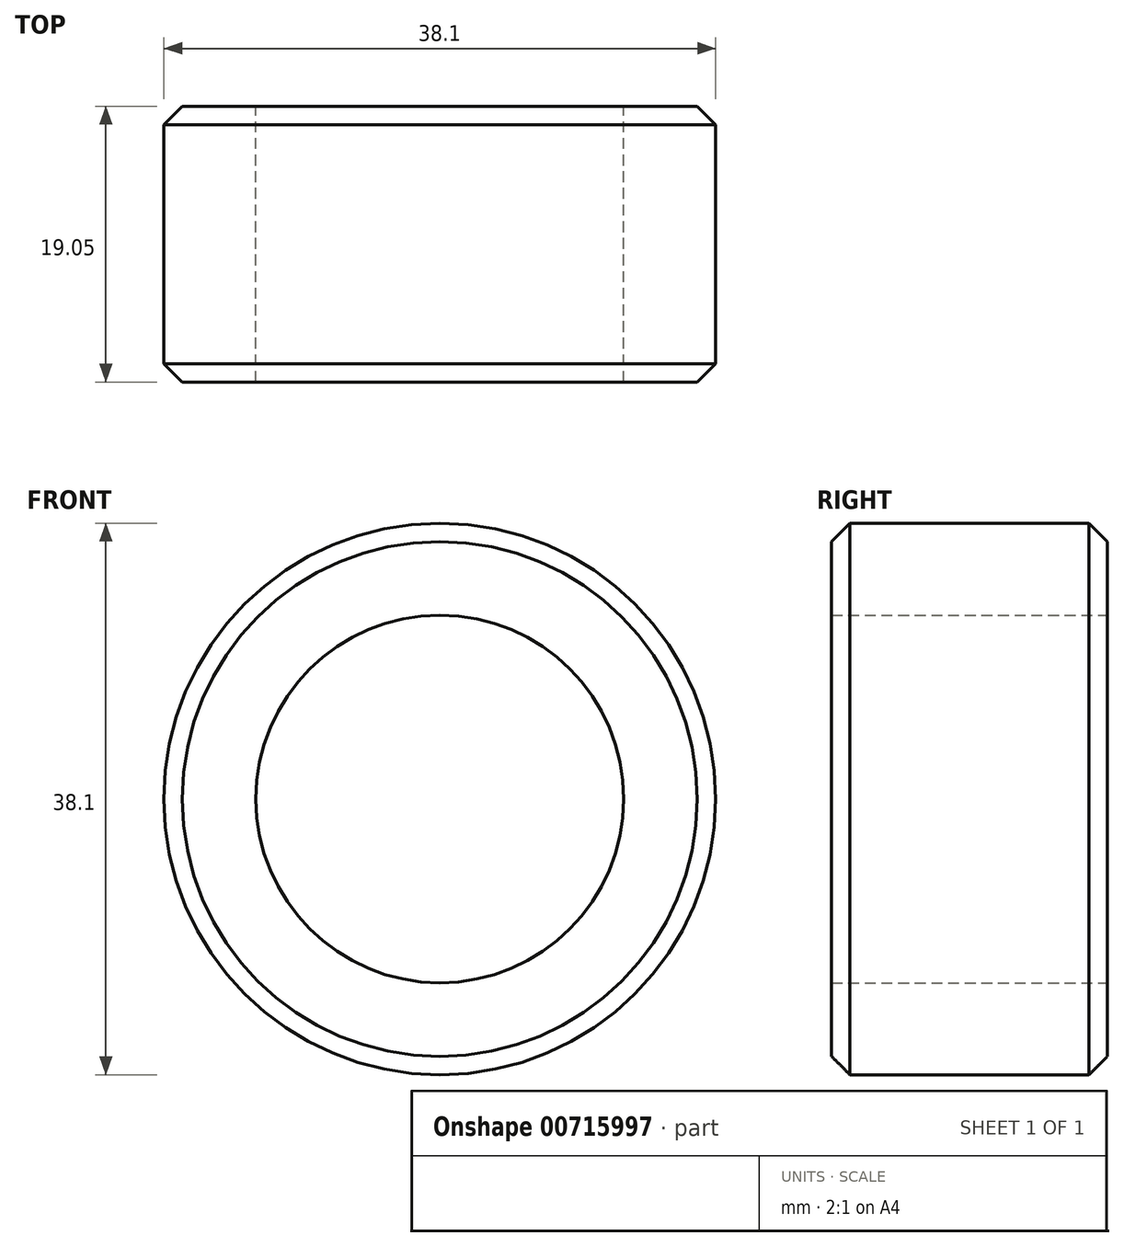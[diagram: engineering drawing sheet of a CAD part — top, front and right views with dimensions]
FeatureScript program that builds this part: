
annotation { "Feature Type Name" : "Feature", "Feature Type Description" : "" }
export const myFeature = defineFeature(function(context is Context, id is Id, definition is map)
    precondition{}
    {
        {
            var Q0;
            Q0=qCreatedBy(makeId("Front.planeOp"),FACE);
            var sketch = newSketch(context, id + "F0", { "sketchPlane" : qUnion([Q0])});
            skCircle(sketch, "E0", {"center": v(0, 0) * mm, "radius": 12.7 * mm});
            skCircle(sketch, "E1", {"center": v(0, 0) * mm, "radius": 19.05 * mm});
            skSolve(sketch);
        }
        {
            var Q0;
            Q0 = qSketchRegion(id + "F0", true);
            var Q1;
            Q1=makeQuery(id+"F0.imprint","IMPRINT",FACE,{"disambiguationData":[TD([[makeQuery(id+"F0.imprint","IMPRINT",EDGE,{"derivedFrom":sQuery(id+"F0.wireOp",EDGE,"E0")}),-1.0]])]});
            extrude(context, id + "F1", {"entities" : qUnion([Q0, Q1]), "depth" : 19.05 * mm, "offsetDistance" : 25.4 * mm});
        }
        {
            var Q0;
            Q0=makeQuery(id+"F1.opExtrude","CAP_EDGE",EDGE,{"disambiguationData":[OSD([sQuery(id+"F0.wireOp",EDGE,"E1")])],"isStart":true});
            var Q1;
            Q1=makeQuery(id+"F1.opExtrude","CAP_EDGE",EDGE,{"disambiguationData":[OSD([sQuery(id+"F0.wireOp",EDGE,"E1")])],"isStart":false});
            chamfer(context, id + "F2", {"entities" : qUnion([Q0, Q1]), "width" : 1.27 * mm, "tangentPropagation" : true});
        }
    });
